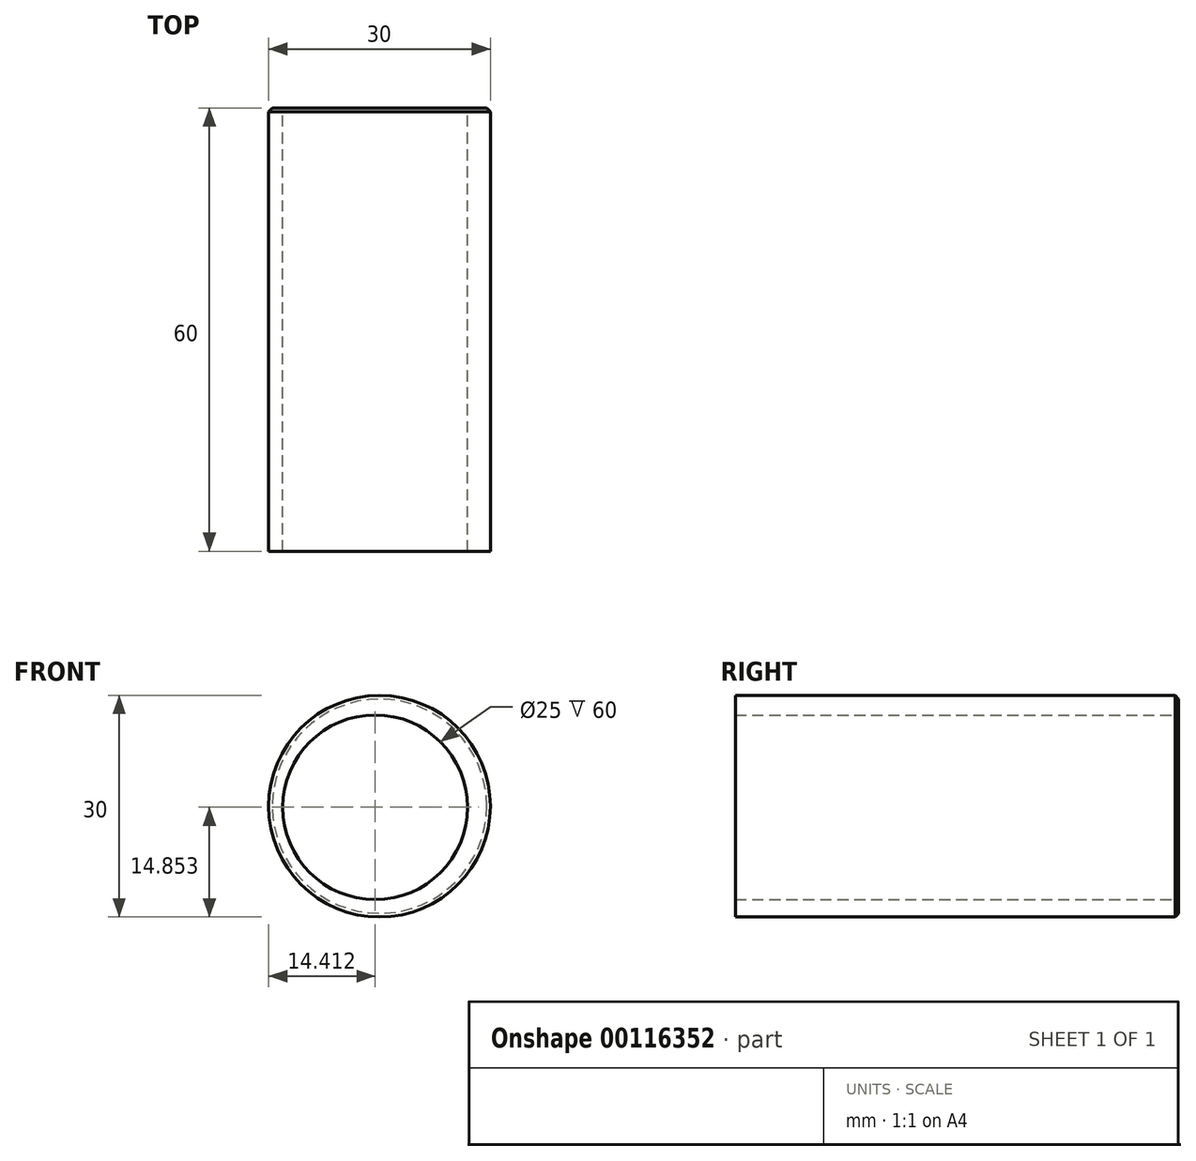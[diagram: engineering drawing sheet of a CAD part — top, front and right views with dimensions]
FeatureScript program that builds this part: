
annotation { "Feature Type Name" : "Feature", "Feature Type Description" : "" }
export const myFeature = defineFeature(function(context is Context, id is Id, definition is map)
    precondition{}
    {
        {
            var Q0;
            Q0=qCreatedBy(makeId("Front.planeOp"),FACE);
            var sketch = newSketch(context, id + "F0", { "sketchPlane" : qUnion([Q0])});
            skCircle(sketch, "E0", {"center": v(0, 0) * mm, "radius": 15 * mm});
            skCircle(sketch, "E1", {"center": v(-0.59, -0.15) * mm, "radius": 12.5 * mm});
            skSolve(sketch);
        }
        {
            var Q0;
            Q0=makeQuery(id+"F0.imprint","IMPRINT",FACE,{"disambiguationData":[TD([[makeQuery(id+"F0.imprint","IMPRINT",EDGE,{"derivedFrom":sQuery(id+"F0.wireOp",EDGE,"E0")}),1.0]])]});
            var Q1;
            Q1=sQuery(id+"F0.wireOp",EDGE,"E1");
            var Q2;
            Q2=sQuery(id+"F0.wireOp",EDGE,"E0");
            extrude(context, id + "F1", {"entities" : qUnion([Q0]), "surfaceEntities" : qUnion([Q1, Q2]), "depth" : 60 * mm});
        }
        {
            var Q0;
            Q0=makeQuery(id+"F1.opExtrude","CAP_EDGE",EDGE,{"disambiguationData":[OSD([sQuery(id+"F0.wireOp",EDGE,"E0")])],"isStart":true});
            chamfer(context, id + "F2", {"entities" : qUnion([Q0]), "width" : .5 * mm, "tangentPropagation" : true});
        }
    });
